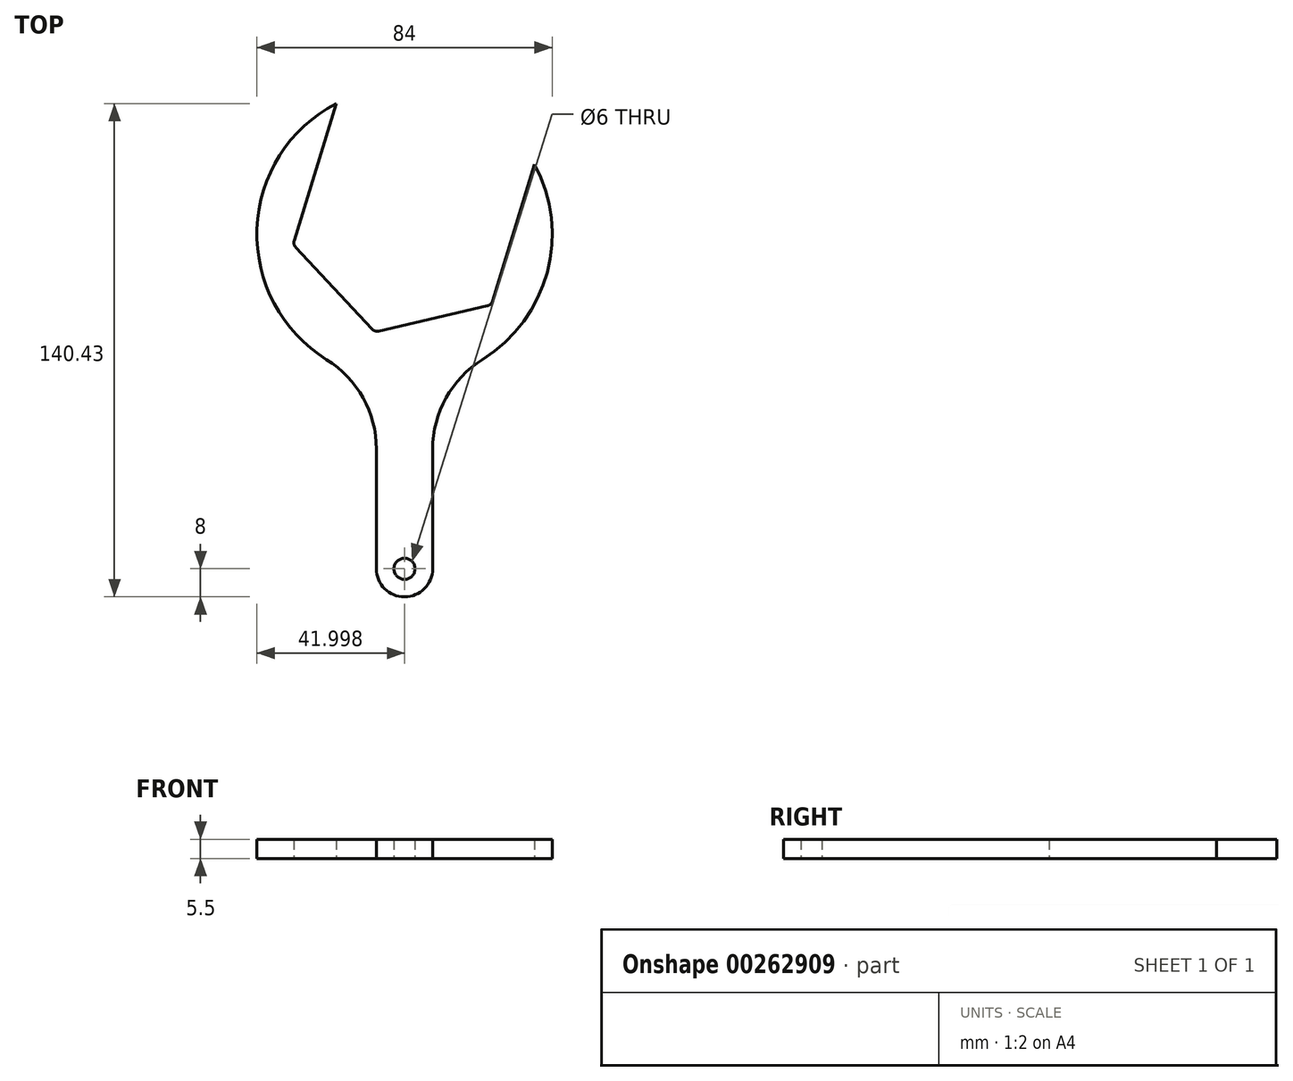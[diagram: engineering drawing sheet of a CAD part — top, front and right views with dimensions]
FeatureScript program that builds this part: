
annotation { "Feature Type Name" : "Feature", "Feature Type Description" : "" }
export const myFeature = defineFeature(function(context is Context, id is Id, definition is map)
    precondition{}
    {
        {
            var Q0;
            Q0=qCreatedBy(makeId("Top.planeOp"),FACE);
            var sketch = newSketch(context, id + "F0", { "sketchPlane" : qUnion([Q0])});
            skCircle(sketch, "E0.cCircle", {"center": v(0, 0) * mm, "radius": 29.5 * mm, "construction": true});
            skLineSegment(sketch, "E0.0", {"start": v(35.49, 15.18) * mm, "end": v(23.57, -23.8) * mm});
            skLineSegment(sketch, "E0.1", {"start": v(22.1, -25.17) * mm, "end": v(-8.83, -32.32) * mm});
            skLineSegment(sketch, "E0.2", {"start": v(-10.75, -31.73) * mm, "end": v(-32.4, -8.5) * mm});
            skLineSegment(sketch, "E0.3", {"start": v(-32.85, -6.56) * mm, "end": v(-20.93, 32.43) * mm});
            skLineSegment(sketch, "E0.4", {"start": v(-23.23, 24.91) * mm, "end": v(9.96, 32.58) * mm, "construction": true});
            skLineSegment(sketch, "E0.5", {"start": v(9.96, 32.58) * mm, "end": v(33.2, 7.66) * mm, "construction": true});
            skPoint(sketch, "E0.0.midPoint", {"position": v(28.21, -8.62) * mm});
            skArc(sketch, "E1", {"start": v(-9.46, -100) * mm, "mid": v(-1.46, -108) * mm, "end": v(6.54, -100) * mm});
            skLineSegment(sketch, "E2.trimOffspring", {"start": v(6.54, -65.94) * mm, "end": v(6.54, -100) * mm});
            skLineSegment(sketch, "E3.trimOffspring", {"start": v(-9.46, -65.94) * mm, "end": v(-9.46, -100) * mm});
            skCircle(sketch, "E4", {"center": v(-1.46, -100) * mm, "radius": 3 * mm});
            skPoint(sketch, "E5.visualSharp", {"position": v(33.2, 7.66) * mm});
            skPoint(sketch, "E6.visualSharp", {"position": v(-23.23, 24.91) * mm});
            skLineSegment(sketch, "E7", {"start": v(-8.62, -28.21) * mm, "end": v(8.62, 28.21) * mm, "construction": true});
            skArc(sketch, "E8", {"start": v(20.7, -40.46) * mm, "mid": v(39.13, -15.57) * mm, "end": v(35.49, 15.18) * mm});
            skArc(sketch, "E9", {"start": v(-9.46, -46.01) * mm, "mid": v(-1.46, -46.78) * mm, "end": v(6.54, -46.01) * mm, "construction": true});
            skLineSegment(sketch, "E10", {"start": v(-1.46, -4.78) * mm, "end": v(-1.46, -100) * mm, "construction": true});
            skLineSegment(sketch, "E11", {"start": v(-20.93, 32.43) * mm, "end": v(-20.93, 32.43) * mm});
            skArc(sketch, "E12", {"start": v(-20.93, 32.43) * mm, "mid": v(-43.43, -3.23) * mm, "end": v(-23.63, -40.46) * mm});
            skArc(sketch, "E13", {"start": v(35.49, 15.18) * mm, "mid": v(10.82, 35.38) * mm, "end": v(-20.93, 32.43) * mm, "construction": true});
            skPoint(sketch, "E14.visualSharp", {"position": v(6.54, -46.01) * mm});
            skArc(sketch, "E14.filletArc", {"start": v(20.7, -40.46) * mm, "mid": v(10.32, -51.36) * mm, "end": v(6.54, -65.94) * mm});
            skPoint(sketch, "E15.visualSharp", {"position": v(-9.46, -46.01) * mm});
            skArc(sketch, "E15.filletArc", {"start": v(-9.46, -65.94) * mm, "mid": v(-13.24, -51.36) * mm, "end": v(-23.63, -40.46) * mm});
            skPoint(sketch, "E16.visualSharp", {"position": v(-33.2, -7.66) * mm});
            skArc(sketch, "E16.filletArc", {"start": v(-32.85, -6.56) * mm, "mid": v(-32.89, -7.6) * mm, "end": v(-32.4, -8.5) * mm});
            skPoint(sketch, "E17.visualSharp", {"position": v(-9.96, -32.58) * mm});
            skArc(sketch, "E17.filletArc", {"start": v(-10.75, -31.73) * mm, "mid": v(-9.87, -32.28) * mm, "end": v(-8.83, -32.32) * mm});
            skPoint(sketch, "E18.visualSharp", {"position": v(23.23, -24.91) * mm});
            skArc(sketch, "E18.filletArc", {"start": v(22.1, -25.17) * mm, "mid": v(23.02, -24.69) * mm, "end": v(23.57, -23.8) * mm});
            skSolve(sketch);
        }
        {
            var Q0;
            Q0=qSketchRegion(id+"F0",true);
            extrude(context, id + "F1", {"entities" : qUnion([Q0]), "depth" : 5.5 * mm});
        }
    });
